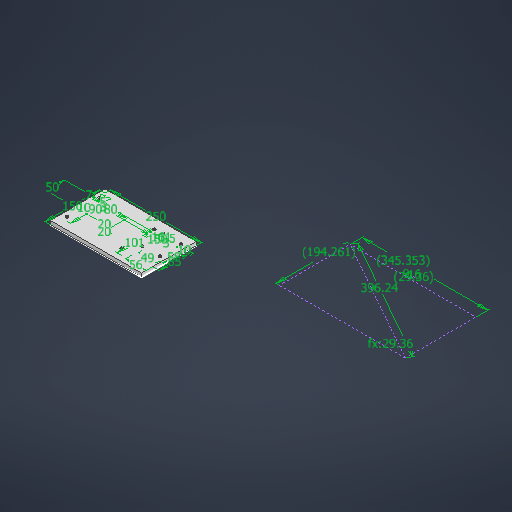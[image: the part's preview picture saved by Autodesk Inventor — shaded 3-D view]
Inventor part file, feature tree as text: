
AUTODESK INVENTOR PART (.ipt)
format: ipt  version: 2025.1 (Build 291241000, 241)  size: 262,144 bytes
history: native  units: mm
features: extrude x2, sketch x1
ambient origin geometry x8: Origin, YZ Plane, XZ Plane, XY Plane, X Axis, Y Axis, Z Axis, Center Point
bodies: Body1 (feature_tree)
feature tree (3):
  sketch  "Sketch1"  dims[d34=396.24mm d37=345.353091mm d39=9.0mm d40=16.0mm d41=5.123895mm d42=5.123895mm d43=194.261114mm d46=161.0mm d47=101.0mm d48=3.0mm d49=150.0mm d50=90.0mm d51=5.0mm d52=20.0mm d53=20.0mm d54=50.0mm d55=80.0mm d56=56.0mm d57=85.0mm d58=49.0mm d59=58.0mm d60=3.0mm d61=3.5mm d64=250.0mm d65=150.0mm d69=10.0mm d70=0.0mm d71=2.0mm d72=0.0mm d73=10.0mm d74=10.0mm d75=7.0mm]
  extrude  "Extrusion2"  Depth=10.0mm
  extrude  "Extrusion3"  Depth=10.0mm
